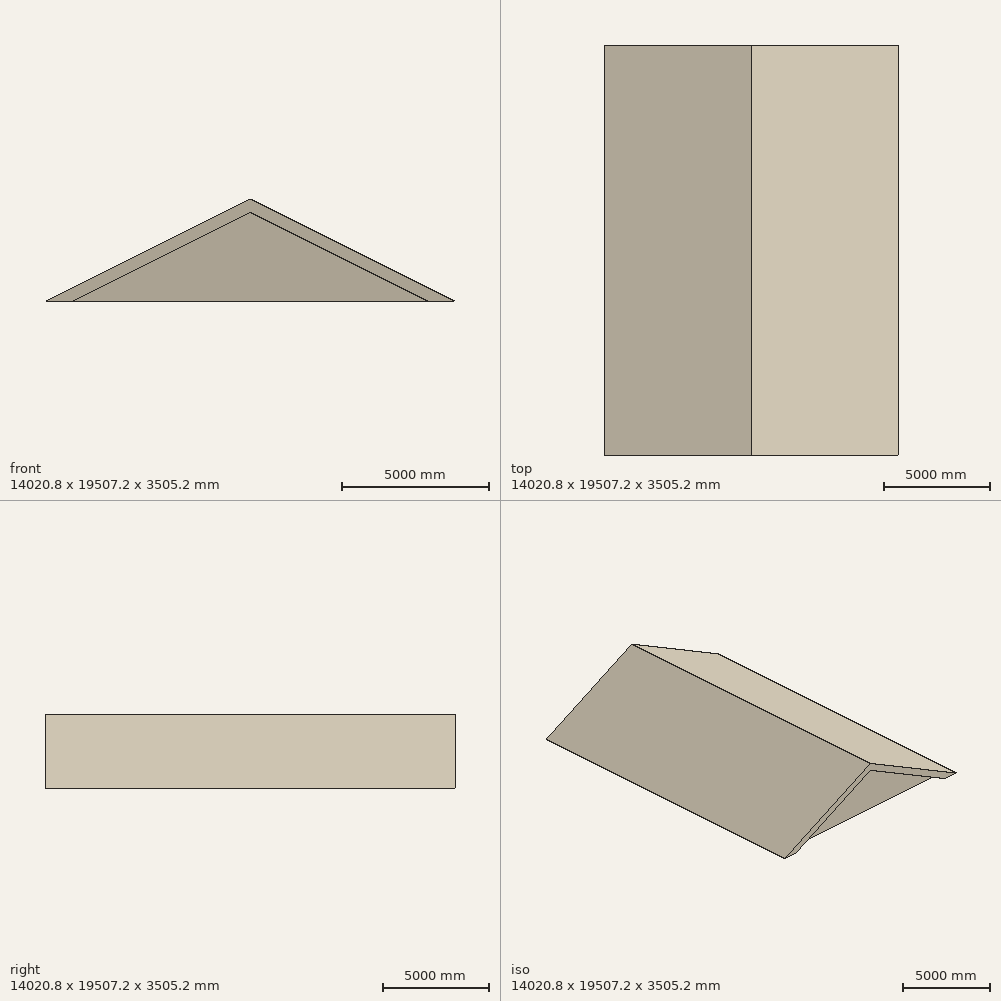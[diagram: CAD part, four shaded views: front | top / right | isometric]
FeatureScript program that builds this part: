
annotation { "Feature Type Name" : "Feature", "Feature Type Description" : "" }
export const myFeature = defineFeature(function(context is Context, id is Id, definition is map)
    precondition{}
    {
        {
            var Q0;
            Q0=qCreatedBy(makeId("Front.planeOp"),FACE);
            var sketch = newSketch(context, id + "F0", { "sketchPlane" : qUnion([Q0])});
            skLineSegment(sketch, "E0", {"start": v(0, 0) * mm, "end": v(-6096, 0) * mm});
            skLineSegment(sketch, "E1", {"start": v(0, 0) * mm, "end": v(6096, 0) * mm});
            skLineSegment(sketch, "E2", {"start": v(0, 0) * mm, "end": v(0, 3048) * mm});
            skLineSegment(sketch, "E3", {"start": v(0, 3048) * mm, "end": v(-6096, 0) * mm});
            skLineSegment(sketch, "E4", {"start": v(0, 3048) * mm, "end": v(6096, 0) * mm});
            skLineSegment(sketch, "E5", {"start": v(-6096, 0) * mm, "end": v(-7010.4, 0) * mm});
            skLineSegment(sketch, "E6", {"start": v(6096, 0) * mm, "end": v(7010.4, 0) * mm});
            skLineSegment(sketch, "E7", {"start": v(0, 3048) * mm, "end": v(0, 3505.2) * mm});
            skLineSegment(sketch, "E8", {"start": v(0, 3505.2) * mm, "end": v(-7010.4, 0) * mm});
            skLineSegment(sketch, "E9", {"start": v(0, 3505.2) * mm, "end": v(7010.4, 0) * mm});
            skLineSegment(sketch, "E10", {"start": v(-6096, 0) * mm, "end": v(-6096, -7315.2) * mm});
            skLineSegment(sketch, "E11", {"start": v(-6096, -7315.2) * mm, "end": v(6096, -7315.2) * mm});
            skLineSegment(sketch, "E12", {"start": v(6096, 0) * mm, "end": v(6096, -7315.2) * mm});
            skLineSegment(sketch, "E13", {"start": v(-6096, -7315.2) * mm, "end": v(-6096, -7620) * mm});
            skLineSegment(sketch, "E14", {"start": v(-6096, -7620) * mm, "end": v(6096, -7620) * mm});
            skLineSegment(sketch, "E15", {"start": v(0, -7315.2) * mm, "end": v(457.2, -7315.2) * mm});
            skLineSegment(sketch, "E16", {"start": v(-457.2, -7315.2) * mm, "end": v(-457.2, -5181.6) * mm});
            skLineSegment(sketch, "E17", {"start": v(-457.2, -5181.6) * mm, "end": v(457.2, -5181.6) * mm});
            skLineSegment(sketch, "E18", {"start": v(457.2, -5181.6) * mm, "end": v(457.2, -7315.2) * mm});
            skLineSegment(sketch, "E19", {"start": v(6096, -7620) * mm, "end": v(6096, -7315.2) * mm});
            skLineSegment(sketch, "E20.bottom", {"start": v(2133.6, -2418.68) * mm, "end": v(5181.6, -2418.68) * mm});
            skLineSegment(sketch, "E20.top", {"start": v(2133.6, -5466.68) * mm, "end": v(5181.6, -5466.68) * mm});
            skLineSegment(sketch, "E20.left", {"start": v(2133.6, -2418.68) * mm, "end": v(2133.6, -5466.68) * mm});
            skLineSegment(sketch, "E20.right", {"start": v(5181.6, -2418.68) * mm, "end": v(5181.6, -5466.68) * mm});
            skLineSegment(sketch, "E21.bottom", {"start": v(-5181.6, -2170.87) * mm, "end": v(-2133.6, -2170.87) * mm});
            skLineSegment(sketch, "E21.top", {"start": v(-5181.6, -5218.87) * mm, "end": v(-2133.6, -5218.87) * mm});
            skLineSegment(sketch, "E21.left", {"start": v(-5181.6, -2170.87) * mm, "end": v(-5181.6, -5218.87) * mm});
            skLineSegment(sketch, "E21.right", {"start": v(-2133.6, -2170.87) * mm, "end": v(-2133.6, -5218.87) * mm});
            skLineSegment(sketch, "E22.0", {"start": v(-5486.4, -1866.07) * mm, "end": v(-1828.8, -1866.07) * mm});
            skLineSegment(sketch, "E22.1", {"start": v(-5486.4, -1866.07) * mm, "end": v(-5486.4, -5523.67) * mm});
            skLineSegment(sketch, "E22.2", {"start": v(-5486.4, -5523.67) * mm, "end": v(-1828.8, -5523.67) * mm});
            skLineSegment(sketch, "E22.3", {"start": v(-1828.8, -1866.07) * mm, "end": v(-1828.8, -5523.67) * mm});
            skLineSegment(sketch, "E23.0", {"start": v(1828.8, -2113.88) * mm, "end": v(5486.4, -2113.88) * mm});
            skLineSegment(sketch, "E23.1", {"start": v(1828.8, -2113.88) * mm, "end": v(1828.8, -5771.48) * mm});
            skLineSegment(sketch, "E23.2", {"start": v(1828.8, -5771.48) * mm, "end": v(5486.4, -5771.48) * mm});
            skLineSegment(sketch, "E23.3", {"start": v(5486.4, -2113.88) * mm, "end": v(5486.4, -5771.48) * mm});
            skSolve(sketch);
        }
        {
            var Q0;
            Q0=makeQuery(id+"F0.imprint","IMPRINT",FACE,{"disambiguationData":[TD([[makeQuery(id+"F0.imprint","IMPRINT",EDGE,{"derivedFrom":sQuery(id+"F0.wireOp",EDGE,"E4")}),1.0]])]});
            var Q1;
            Q1=makeQuery(id+"F0.imprint","IMPRINT",FACE,{"disambiguationData":[TD([[makeQuery(id+"F0.imprint","IMPRINT",EDGE,{"derivedFrom":sQuery(id+"F0.wireOp",EDGE,"E3")}),-1.0]])]});
            extrude(context, id + "F1", {"entities" : qUnion([Q0, Q1]), "endBound" : BoundingType.SYMMETRIC, "depth" : 19507.2 * mm, "offsetDistance" : 30.48 * mm});
        }
        {
            var Q0;
            Q0=makeQuery(id+"F0.imprint","IMPRINT",FACE,{"disambiguationData":[TD([[makeQuery(id+"F0.imprint","IMPRINT",EDGE,{"derivedFrom":sQuery(id+"F0.wireOp",EDGE,"E0")}),-1.0]])]});
            var Q1;
            Q1=makeQuery(id+"F0.imprint","IMPRINT",FACE,{"disambiguationData":[TD([[makeQuery(id+"F0.imprint","IMPRINT",EDGE,{"derivedFrom":sQuery(id+"F0.wireOp",EDGE,"E1")}),1.0]])]});
            extrude(context, id + "F2", {"entities" : qUnion([Q0, Q1]), "operationType" : NewBodyOperationType.ADD, "endBound" : BoundingType.SYMMETRIC, "depth" : 18288 * mm, "offsetDistance" : 30.48 * mm});
        }
    });
